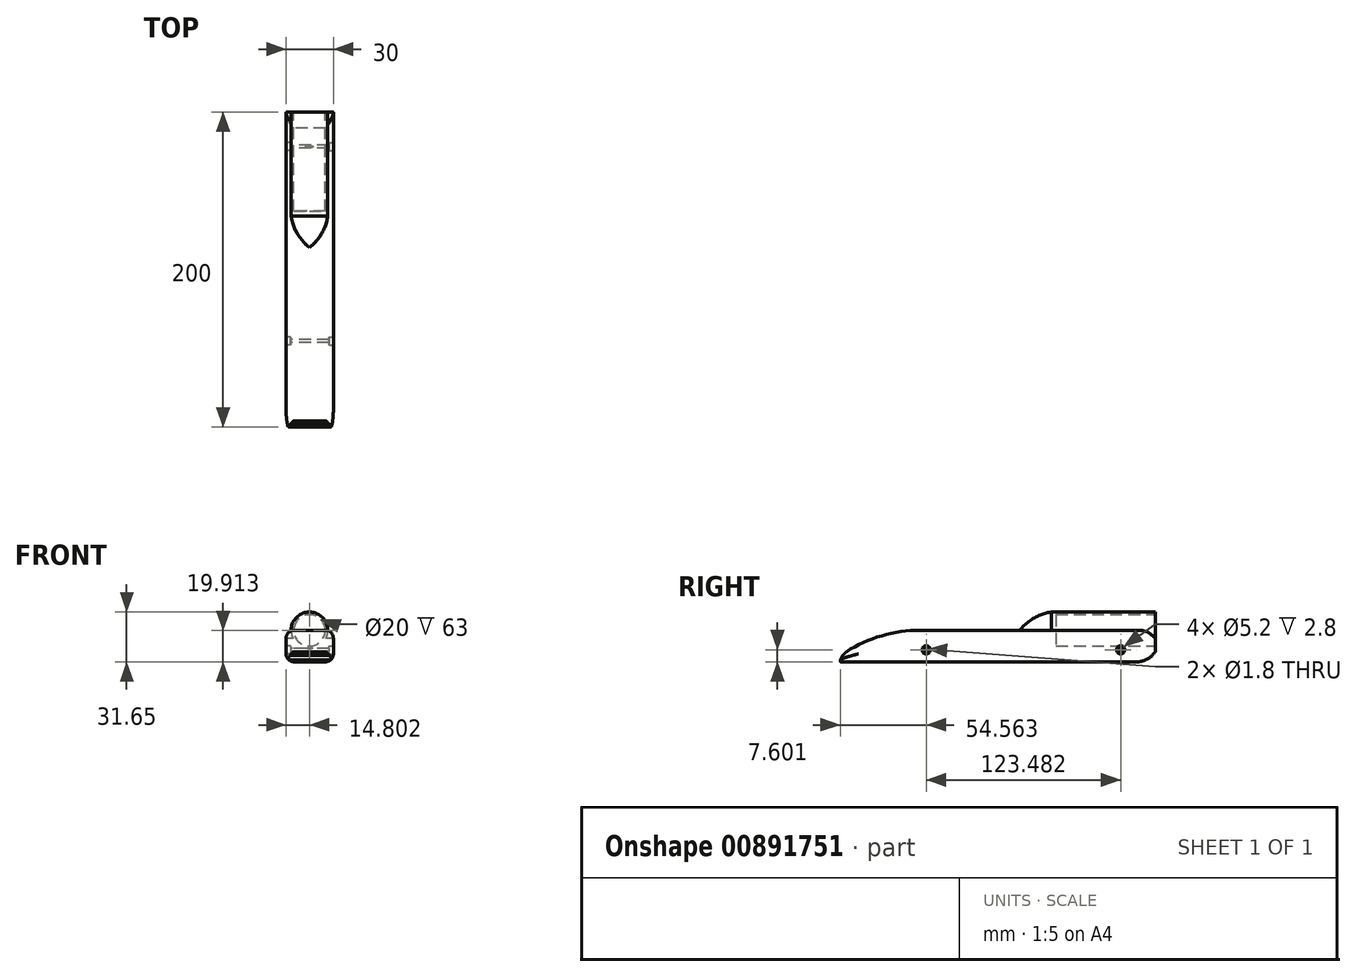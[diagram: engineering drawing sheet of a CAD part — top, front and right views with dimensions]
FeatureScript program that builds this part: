
annotation { "Feature Type Name" : "Feature", "Feature Type Description" : "" }
export const myFeature = defineFeature(function(context is Context, id is Id, definition is map)
    precondition{}
    {
        {
            var Q0;
            Q0=qCreatedBy(makeId("Right.planeOp"),FACE);
            var sketch = newSketch(context, id + "F0", { "sketchPlane" : qUnion([Q0])});
            skLineSegment(sketch, "E0.bottom", {"start": v(89.71, -10) * mm, "end": v(-37.4, -10) * mm});
            skLineSegment(sketch, "E0.top", {"start": v(90.1, 10) * mm, "end": v(-49.28, 10) * mm});
            skLineSegment(sketch, "E0.left", {"start": v(100, -3.63) * mm, "end": v(100, 4.7) * mm});
            skPoint(sketch, "E0.middle", {"position": v(0, 0) * mm});
            skArc(sketch, "E1", {"start": v(-32.94, 10) * mm, "mid": v(-41.11, 10.16) * mm, "end": v(-49.28, 10) * mm});
            skArc(sketch, "E2", {"start": v(-37.4, -10) * mm, "mid": v(-35.18, -10.01) * mm, "end": v(-32.94, -10) * mm});
            skPoint(sketch, "E3.orphan", {"position": v(-100, 10) * mm});
            skPoint(sketch, "E4.orphan", {"position": v(-100, -10) * mm});
            skCircle(sketch, "E5", {"center": v(78.04, -2.4) * mm, "radius": 0.9 * mm});
            skCircle(sketch, "E6", {"center": v(-45.44, -2.4) * mm, "radius": 0.9 * mm});
            skArc(sketch, "E7", {"start": v(100, 4.7) * mm, "mid": v(95.32, 8.7) * mm, "end": v(89.32, 10) * mm});
            skArc(sketch, "E8", {"start": v(89.71, -10) * mm, "mid": v(95.52, -7.9) * mm, "end": v(100, -3.63) * mm});
            skPoint(sketch, "E9.orphan", {"position": v(100, 10) * mm});
            skPoint(sketch, "E10.orphan", {"position": v(100, -10) * mm});
            skLineSegment(sketch, "E11", {"start": v(-37.4, -10) * mm, "end": v(-100, -10) * mm});
            skPoint(sketch, "E0.right.start.orphan", {"position": v(-100, 0) * mm});
            skArc(sketch, "E12", {"start": v(-49.28, 10) * mm, "mid": v(-75.9, 5.84) * mm, "end": v(-100, -6.23) * mm});
            skLineSegment(sketch, "E13", {"start": v(-100, -6.23) * mm, "end": v(-100, -10) * mm});
            skSolve(sketch);
        }
        {
            var Q0;
            {var subQ4=sQuery(id+"F0.wireOp",EDGE,"E0.left");Q0=makeQuery(id+"F0.imprint","IMPRINT",FACE,{"disambiguationData":[TD([[makeQuery(id+"F0.imprint","IMPRINT",EDGE,{"derivedFrom":subQ4}),1.0]])]});}
            extrude(context, id + "F1", {"entities" : qUnion([Q0]), "depth" : 30 * mm, "offsetDistance" : 25 * mm});
        }
        {
            var Q0;
            Q0=makeQuery(id+"F1.opExtrude","SWEPT_FACE",FACE,{"disambiguationData":[OSD([sQuery(id+"F0.wireOp",EDGE,"E0.left")])]});
            var sketch = newSketch(context, id + "F2", { "sketchPlane" : qUnion([Q0])});
            skCircle(sketch, "E14", {"center": v(-14.8, 9.91) * mm, "radius": 11.67 * mm});
            skSolve(sketch);
        }
        {
            var Q0;
            Q0 = qSketchRegion(id + "F2", true);
            extrude(context, id + "F3", {"entities" : qUnion([Q0]), "operationType" : NewBodyOperationType.ADD, "oppositeDirection" : true, "depth" : 66 * mm, "offsetDistance" : 25 * mm});
        }
        {
            var Q0;
            Q0=makeQuery(id+"F3.opExtrude","CAP_FACE",FACE,{"disambiguationData":[OSD([sQuery(id+"F2.wireOp",EDGE,"E14")])],"isStart":true});
            var sketch = newSketch(context, id + "F4", { "sketchPlane" : qUnion([Q0])});
            skCircle(sketch, "E15", {"center": v(-14.8, 9.91) * mm, "radius": 10 * mm});
            skSolve(sketch);
        }
        {
            var Q0;
            Q0 = qSketchRegion(id + "F4", true);
            extrude(context, id + "F5", {"entities" : qUnion([Q0]), "operationType" : NewBodyOperationType.REMOVE, "oppositeDirection" : true, "depth" : 63 * mm, "offsetDistance" : 25 * mm});
        }
        {
            var Q0;
            Q0=makeQuery(id+"F1.opExtrude","SWEPT_FACE",FACE,{"disambiguationData":[OSD([sQuery(id+"F0.wireOp",EDGE,"E0.top")])]});
            var sketch = newSketch(context, id + "F6", { "sketchPlane" : qUnion([Q0])});
            skLineSegment(sketch, "E16", {"start": v(14.8, 34) * mm, "end": v(14.8, 14) * mm});
            skLineSegment(sketch, "E17", {"start": v(14.8, 34) * mm, "end": v(3.15, 34) * mm});
            skArc(sketch, "E18", {"start": v(3.15, 34) * mm, "mid": v(7.06, 22.88) * mm, "end": v(14.8, 14) * mm});
            skSolve(sketch);
        }
        {
            var Q0;
            {var subQ0=sQuery(id+"F6.wireOp",EDGE,"E16");Q0=makeQuery(id+"F6.imprint","IMPRINT",FACE,{"disambiguationData":[TD([[makeQuery(id+"F6.imprint","IMPRINT",EDGE,{"derivedFrom":subQ0}),-1.0]])]});}
            var Q1;
            Q1=sQuery(id+"F6.wireOp",EDGE,"E16");
            revolve(context, id + "F7", {"operationType" : NewBodyOperationType.ADD, "surfaceOperationType" : NewSurfaceOperationType.NEW, "entities" : qUnion([Q0]), "axis" : qUnion([Q1]), "revolveType" : RevolveType.FULL});
        }
        {
            var Q0;
            Q0=makeQuery(id+"F1.opExtrude","SWEPT_EDGE",EDGE,{"disambiguationData":[OSD([sQuery(id+"F0.wireOp",EDGE,"E12"),sQuery(id+"F0.wireOp",EDGE,"E13")])]});
            chamfer(context, id + "F8", {"entities" : qUnion([Q0]), "width" : 5 * mm, "tangentPropagation" : true});
        }
        {
            var Q0;
            {var subQ0=sQuery(id+"F0.wireOp",EDGE,"E12");Q0=makeQuery(id+"F8.opChamfer","BLEND_EDGE",EDGE,{"blendedFrom":[makeQuery(id+"F1.opExtrude","SWEPT_EDGE",EDGE,{"disambiguationData":[OSD([subQ0,sQuery(id+"F0.wireOp",EDGE,"E13")])]}),makeQuery(id+"F1.opExtrude","SWEPT_FACE",FACE,{"disambiguationData":[OSD([subQ0])]})],"blendedInto":[makeQuery(id+"F1.opExtrude","SWEPT_FACE",FACE,{"disambiguationData":[OSD([subQ0])]})]});}
            chamfer(context, id + "F9", {"entities" : qUnion([Q0]), "width" : 5 * mm, "tangentPropagation" : true});
        }
        {
            var Q0;
            {var subQ0=sQuery(id+"F0.wireOp",EDGE,"E12");var subQ1=makeQuery(id+"F1.opExtrude","SWEPT_FACE",FACE,{"disambiguationData":[OSD([subQ0])]});Q0=makeQuery(id+"F9.opChamfer","BLEND_EDGE",EDGE,{"blendedFrom":[makeQuery(id+"F8.opChamfer","BLEND_EDGE",EDGE,{"blendedFrom":[makeQuery(id+"F1.opExtrude","SWEPT_EDGE",EDGE,{"disambiguationData":[OSD([subQ0,sQuery(id+"F0.wireOp",EDGE,"E13")])]}),subQ1],"blendedInto":[subQ1]}),subQ1],"blendedInto":[subQ1]});}
            chamfer(context, id + "F10", {"entities" : qUnion([Q0]), "width" : 5 * mm, "tangentPropagation" : true});
        }
        {
            var Q0;
            Q0=makeQuery(id+"F1.opExtrude","CAP_EDGE",EDGE,{"disambiguationData":[OSD([sQuery(id+"F0.wireOp",EDGE,"E0.bottom"),sQuery(id+"F0.wireOp",EDGE,"E11")])],"isStart":false});
            var Q1;
            Q1=makeQuery(id+"F1.opExtrude","CAP_EDGE",EDGE,{"disambiguationData":[OSD([sQuery(id+"F0.wireOp",EDGE,"E0.bottom"),sQuery(id+"F0.wireOp",EDGE,"E11")])],"isStart":true});
            fillet(context, id + "F11", {"entities" : qUnion([Q0, Q1]), "radius" : 5 * mm, "tangentPropagation" : true, "allowEdgeOverflow" : false});
        }
        {
            var Q0;
            Q0=makeQuery(id+"F1.opExtrude","CAP_EDGE",EDGE,{"disambiguationData":[OSD([sQuery(id+"F0.wireOp",EDGE,"E0.top")])],"isStart":true});
            var Q1;
            Q1=makeQuery(id+"F1.opExtrude","CAP_EDGE",EDGE,{"disambiguationData":[OSD([sQuery(id+"F0.wireOp",EDGE,"E0.top")])],"isStart":false});
            fillet(context, id + "F12", {"entities" : qUnion([Q0, Q1]), "radius" : 5 * mm, "tangentPropagation" : true, "allowEdgeOverflow" : false});
        }
        {
            var Q0;
            Q0=makeQuery(id+"F1.opExtrude","CAP_FACE",FACE,{"disambiguationData":[OSD([sQuery(id+"F0.wireOp",EDGE,"E0.bottom"),sQuery(id+"F0.wireOp",EDGE,"E0.top"),sQuery(id+"F0.wireOp",EDGE,"E0.left"),sQuery(id+"F0.wireOp",EDGE,"E5"),sQuery(id+"F0.wireOp",EDGE,"E6"),sQuery(id+"F0.wireOp",EDGE,"E7"),sQuery(id+"F0.wireOp",EDGE,"E8"),sQuery(id+"F0.wireOp",EDGE,"E11"),sQuery(id+"F0.wireOp",EDGE,"E12"),sQuery(id+"F0.wireOp",EDGE,"E13")])],"isStart":false});
            var sketch = newSketch(context, id + "F13", { "sketchPlane" : qUnion([Q0])});
            skCircle(sketch, "E19", {"center": v(-45.44, -2.4) * mm, "radius": 2.6 * mm});
            skSolve(sketch);
        }
        {
            var Q0;
            Q0 = qSketchRegion(id + "F13", true);
            extrude(context, id + "F14", {"entities" : qUnion([Q0]), "operationType" : NewBodyOperationType.REMOVE, "oppositeDirection" : true, "depth" : 2.8 * mm, "offsetDistance" : 25 * mm});
        }
        {
            var Q0;
            Q0=makeQuery(id+"F1.opExtrude","CAP_FACE",FACE,{"disambiguationData":[OSD([sQuery(id+"F0.wireOp",EDGE,"E0.bottom"),sQuery(id+"F0.wireOp",EDGE,"E0.top"),sQuery(id+"F0.wireOp",EDGE,"E0.left"),sQuery(id+"F0.wireOp",EDGE,"E5"),sQuery(id+"F0.wireOp",EDGE,"E6"),sQuery(id+"F0.wireOp",EDGE,"E7"),sQuery(id+"F0.wireOp",EDGE,"E8"),sQuery(id+"F0.wireOp",EDGE,"E11"),sQuery(id+"F0.wireOp",EDGE,"E12"),sQuery(id+"F0.wireOp",EDGE,"E13")])],"isStart":false});
            var sketch = newSketch(context, id + "F15", { "sketchPlane" : qUnion([Q0])});
            skCircle(sketch, "E20", {"center": v(78.04, -2.4) * mm, "radius": 2.6 * mm});
            skSolve(sketch);
        }
        {
            var Q0;
            Q0 = qSketchRegion(id + "F15", true);
            extrude(context, id + "F16", {"entities" : qUnion([Q0]), "operationType" : NewBodyOperationType.REMOVE, "oppositeDirection" : true, "depth" : 2.8 * mm, "offsetDistance" : 25 * mm});
        }
        {
            var Q0;
            Q0=makeQuery(id+"F1.opExtrude","CAP_FACE",FACE,{"disambiguationData":[OSD([sQuery(id+"F0.wireOp",EDGE,"E0.bottom"),sQuery(id+"F0.wireOp",EDGE,"E0.top"),sQuery(id+"F0.wireOp",EDGE,"E0.left"),sQuery(id+"F0.wireOp",EDGE,"E5"),sQuery(id+"F0.wireOp",EDGE,"E6"),sQuery(id+"F0.wireOp",EDGE,"E7"),sQuery(id+"F0.wireOp",EDGE,"E8"),sQuery(id+"F0.wireOp",EDGE,"E11"),sQuery(id+"F0.wireOp",EDGE,"E12"),sQuery(id+"F0.wireOp",EDGE,"E13")])],"isStart":true});
            var sketch = newSketch(context, id + "F17", { "sketchPlane" : qUnion([Q0])});
            skCircle(sketch, "E21", {"center": v(-78.04, -2.4) * mm, "radius": 2.6 * mm});
            skSolve(sketch);
        }
        {
            var Q0;
            Q0 = qSketchRegion(id + "F17", true);
            extrude(context, id + "F18", {"entities" : qUnion([Q0]), "operationType" : NewBodyOperationType.REMOVE, "oppositeDirection" : true, "depth" : 2.8 * mm, "offsetDistance" : 25 * mm});
        }
        {
            var Q0;
            Q0=makeQuery(id+"F1.opExtrude","CAP_FACE",FACE,{"disambiguationData":[OSD([sQuery(id+"F0.wireOp",EDGE,"E0.bottom"),sQuery(id+"F0.wireOp",EDGE,"E0.top"),sQuery(id+"F0.wireOp",EDGE,"E0.left"),sQuery(id+"F0.wireOp",EDGE,"E5"),sQuery(id+"F0.wireOp",EDGE,"E6"),sQuery(id+"F0.wireOp",EDGE,"E7"),sQuery(id+"F0.wireOp",EDGE,"E8"),sQuery(id+"F0.wireOp",EDGE,"E11"),sQuery(id+"F0.wireOp",EDGE,"E12"),sQuery(id+"F0.wireOp",EDGE,"E13")])],"isStart":true});
            var sketch = newSketch(context, id + "F19", { "sketchPlane" : qUnion([Q0])});
            skCircle(sketch, "E22", {"center": v(45.44, -2.4) * mm, "radius": 2.6 * mm});
            skSolve(sketch);
        }
        {
            var Q0;
            Q0 = qSketchRegion(id + "F19", true);
            extrude(context, id + "F20", {"entities" : qUnion([Q0]), "operationType" : NewBodyOperationType.REMOVE, "oppositeDirection" : true, "depth" : 2.8 * mm, "offsetDistance" : 25 * mm});
        }
    });
